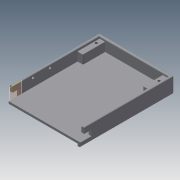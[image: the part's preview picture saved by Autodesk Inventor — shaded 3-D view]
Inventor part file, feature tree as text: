
AUTODESK INVENTOR PART (.ipt)
format: ipt  version: 2019 (Build 230136000, 136)  size: 352,768 bytes
history: native  units: mm
features: extrude x7, sketch x7, other x5, fillet x2, plane x2, projected_geometry x2, surface_op x1
ambient origin geometry x8: Origin, YZ Plane, XZ Plane, XY Plane, X Axis, Y Axis, Z Axis, Center Point
bodies: Solid1 (feature_tree)
feature tree (26):
  extrude  "Extrusion1"  Depth=170.0mm
  extrude  "Extrusion2"  Depth=5.0mm
  extrude  "Extrusion3"  Depth=2.0mm TaperAngle=0.0deg
  fillet  "Fillet1"  Radius=2.0mm
  extrude  "Extrusion4"  TaperAngle=0.0deg  [1 undecoded]
  extrude  "Extrusion5"  Depth=40.0mm
  fillet  "Fillet2"  [1 undecoded]
  plane  "Work Plane2"
  extrude  "Extrusion7"  Depth=35.0mm
  plane  "Work Plane1"
  extrude  "Extrusion8"  Depth=16.0mm TaperAngle=0.0deg
  surface_op  "Sculpt3"
  sketch  "Sketch1"  dims[d0=135.0mm d1=170.0mm]
  sketch  "Sketch2"  dims[d2=28.0mm d3=0.0mm d4=5.0mm]
  projected_geometry  "Projected Loop1"
  sketch  "Sketch3"  dims[d5=20.0mm d6=0.0mm d7=25.0mm d8=0.0mm d9=2.0mm]
  projected_geometry  "Projected Loop2"
  sketch  "Sketch4"  dims[d10=0.0mm d11=0.0mm]
  sketch  "Sketch5"  dims[d12=10.0mm d13=40.0mm d14=0.0mm]
  sketch  "Sketch6"  dims[d15=0.0mm d16=35.0mm]
  sketch  "Sketch7"  dims[d17=11.0mm d18=16.0mm d19=0.0mm d20=4.5mm d22=4.0mm d23=4.5mm d24=6.5mm d26=12.0mm d27=0.0mm d28=1.0mm d29=4.5mm d30=4.5mm d31=30.8mm d32=5.0mm d34=90.0mm d37=0.0mm d38=0.0mm d39=-1.5mm d40=7.5mm d41=7.5mm d42=3.15mm d43=0.0mm d44=10.0mm d45=12.5mm]
  other  "Composite3"
  other  "Srf3"
  parser-record x1  (decoder bookkeeping rows leaked as tree rows — omitted from the tree; the rows remain in map.json)
  other  "CaseA.iam"
  other  "Case_A1:1"
note: 2 required parameter values undecoded (feature->parameter linkage not recoverable at this tier; creation-order binding heuristic only, values carry confidence <= 0.55)
note: 1 file-system path scrubbed to <path> (originals preserved in map.json)
